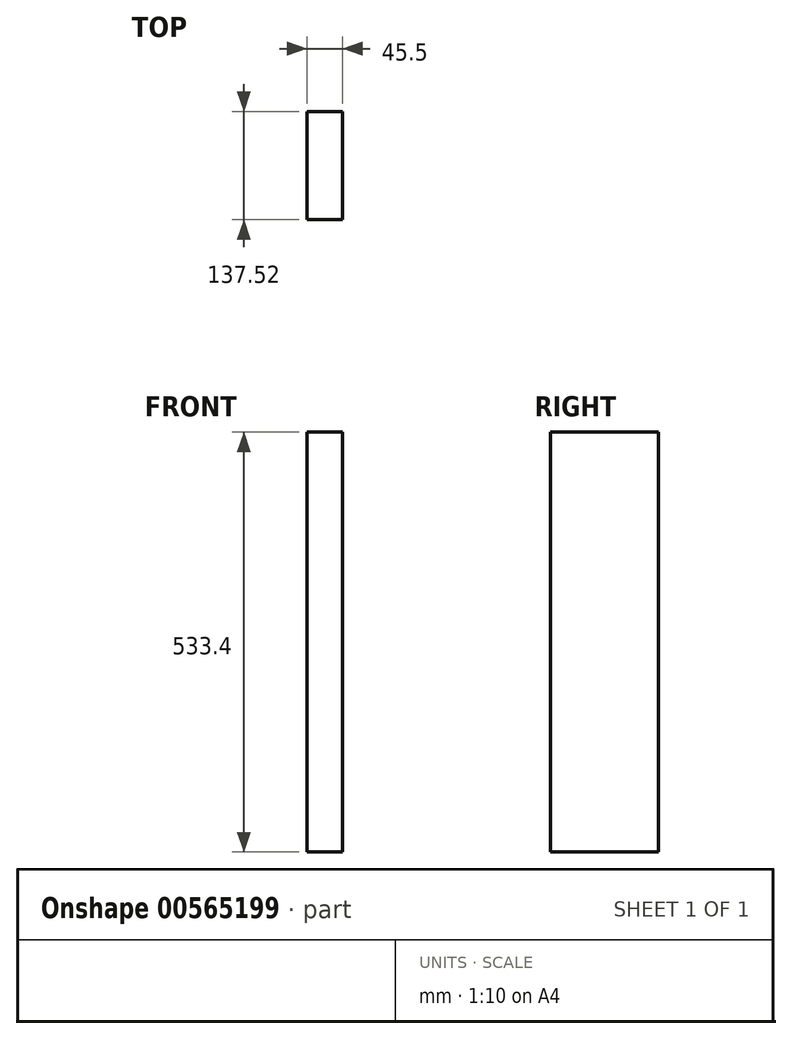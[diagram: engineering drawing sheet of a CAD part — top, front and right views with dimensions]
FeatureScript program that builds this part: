
annotation { "Feature Type Name" : "Feature", "Feature Type Description" : "" }
export const myFeature = defineFeature(function(context is Context, id is Id, definition is map)
    precondition{}
    {
        {
            var Q0;
            Q0=qCreatedBy(makeId("Top.planeOp"),FACE);
            var sketch = newSketch(context, id + "F0", { "sketchPlane" : qUnion([Q0])});
            skLineSegment(sketch, "E0.bottom", {"start": v(-40.58, 39.76) * mm, "end": v(4.92, 39.76) * mm});
            skLineSegment(sketch, "E0.top", {"start": v(-40.58, -97.76) * mm, "end": v(4.92, -97.76) * mm});
            skLineSegment(sketch, "E0.left", {"start": v(-40.58, 39.76) * mm, "end": v(-40.58, -97.76) * mm});
            skLineSegment(sketch, "E0.right", {"start": v(4.92, 39.76) * mm, "end": v(4.92, -97.76) * mm});
            skSolve(sketch);
        }
        {
            var Q0;
            Q0 = qSketchRegion(id + "F0", true);
            extrude(context, id + "F1", {"entities" : qUnion([Q0]), "depth" : 533.4 * mm, "offsetDistance" : 25.4 * mm});
        }
    });
